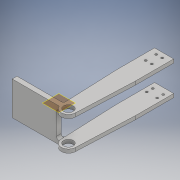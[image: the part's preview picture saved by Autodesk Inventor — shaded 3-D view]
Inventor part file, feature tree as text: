
AUTODESK INVENTOR PART (.ipt)
format: ipt  version: 2017 (Build 210142000, 142)  size: 225,280 bytes
history: native  units: in
note: dims shown in document units (in); Inventor stores cm internally (conversion verified against a paired STEP export)
features: sketch x7, projected_geometry x7, extrude x4, hole x3, plane x2, fillet x2
ambient origin geometry x8: Origin, YZ Plane, XZ Plane, XY Plane, X Axis, Y Axis, Z Axis, Center Point
bodies: Solid1 (feature_tree)
feature tree (25):
  sketch  "Sketch1"  dims[d0=5.0in d1=1.0in]
  plane  "Work Plane1"
  extrude  "Extrusion2"  Depth=1.0in
  plane  "Work Plane2"
  extrude  "Extrusion3"  Depth=1.0in
  hole  "Hole2"  [1 undecoded]
  extrude  "Extrusion4"  Depth=1.753in
  extrude  "Extrusion5"  Depth=1.753in
  fillet  "Fillet1"  Radius=2.0in
  fillet  "Fillet2"  Radius=1.753in
  hole  "Hole3"  [1 undecoded]
  hole  "Hole4"  [1 undecoded]
  sketch  "Sketch2"  dims[d5=1.0in d6=0.75in]
  projected_geometry  "Projected Loop1"
  sketch  "Sketch4"  dims[d7=0.5in d8=0.0in]
  projected_geometry  "Projected Loop3"
  sketch  "Sketch5"  dims[d9=1.753in d10=0.0in d18=0.75in]
  projected_geometry  "Projected Loop4"
  sketch  "Sketch8"  dims[d19=0.125in d20=2.0in d21=2.0in d22=1.753in d23=0.0in]
  projected_geometry  "Projected Loop9"
  projected_geometry  "Projected Loop10"
  sketch  "Sketch9"  dims[d24=0.505in d25=0.75in d26=0.375in d27=0.25in d28=0.5635in d29=1.0in d30=0.8108in d31=2.5in]
  projected_geometry  "Projected Loop11"
  sketch  "Sketch10"  dims[d32=0.25in d33=0.375in d34=0.3125in d35=5.0in d36=4.875in d37=1.753in d38=0.0in d41=1.753in d42=5.375in d43=1.378in d44=0.1875in d45=5.875in d46=1.0in d47=0.0in d48=0.125in d49=0.125in d50=0.6299in d51=1.0in d52=0.5in d53=0.315in d54=0.1575in d55=0.117in d56=0.75in d57=0.375in d58=0.25in d59=0.5635in d60=1.0in d61=0.8108in d62=0.6299in d63=1.0in d64=0.5in d65=0.315in d66=0.1575in d67=0.117in d68=0.75in d69=0.375in d70=0.25in d71=0.5635in d72=1.0in d73=0.8108in]
  projected_geometry  "Projected Loop12"
note: 3 required parameter values undecoded (feature->parameter linkage not recoverable at this tier; creation-order binding heuristic only, values carry confidence <= 0.55)
